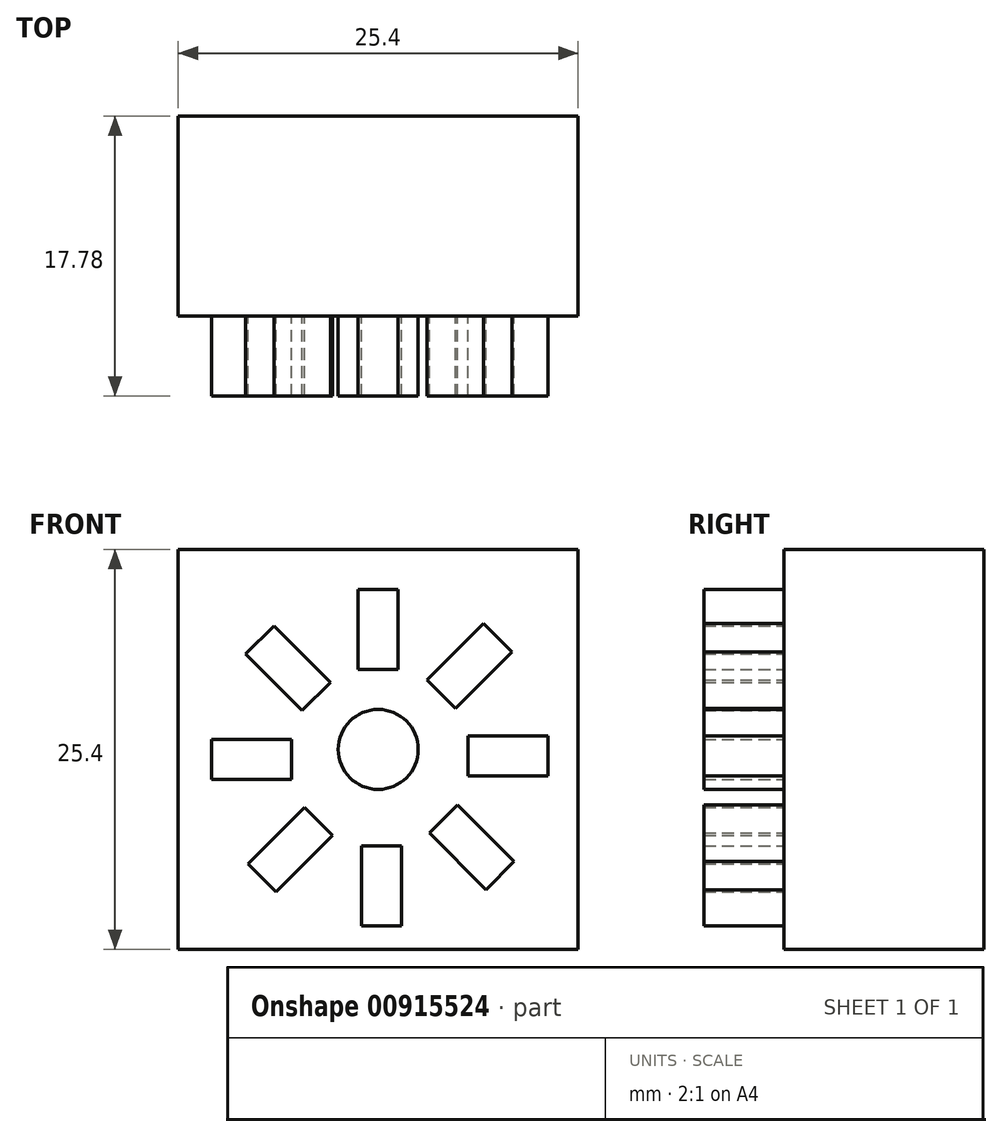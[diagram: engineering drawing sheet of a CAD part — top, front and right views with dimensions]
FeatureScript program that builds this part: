
annotation { "Feature Type Name" : "Feature", "Feature Type Description" : "" }
export const myFeature = defineFeature(function(context is Context, id is Id, definition is map)
    precondition{}
    {
        {
            var Q0;
            Q0=qCreatedBy(makeId("Front.planeOp"),FACE);
            var sketch = newSketch(context, id + "F0", { "sketchPlane" : qUnion([Q0])});
            skLineSegment(sketch, "E0.bottom", {"start": v(5.5, 14.4) * mm, "end": v(-19.9, 14.4) * mm});
            skLineSegment(sketch, "E0.top", {"start": v(5.5, -11) * mm, "end": v(-19.9, -11) * mm});
            skLineSegment(sketch, "E0.left", {"start": v(5.5, 14.4) * mm, "end": v(5.5, -11) * mm});
            skLineSegment(sketch, "E0.right", {"start": v(-19.9, 14.4) * mm, "end": v(-19.9, -11) * mm});
            skSolve(sketch);
        }
        {
            var Q0;
            Q0 = qSketchRegion(id + "F0", true);
            extrude(context, id + "F1", {"entities" : qUnion([Q0]), "depth" : 12.7 * mm, "offsetDistance" : 25.4 * mm});
        }
        {
            var Q0;
            Q0=qCreatedBy(makeId("Front.planeOp"),FACE);
            var sketch = newSketch(context, id + "F2", { "sketchPlane" : qUnion([Q0])});
            skLineSegment(sketch, "E1", {"start": v(-7.2, 14.4) * mm, "end": v(-7.2, -12.07) * mm, "construction": true});
            skLineSegment(sketch, "E2", {"start": v(-32.91, 1.7) * mm, "end": v(5.5, 1.7) * mm, "construction": true});
            skSolve(sketch);
        }
        {
            var Q0;
            Q0=makeQuery(id+"F1.opExtrude","CAP_FACE",FACE,{"disambiguationData":[OSD([sQuery(id+"F0.wireOp",EDGE,"E0.bottom"),sQuery(id+"F0.wireOp",EDGE,"E0.top"),sQuery(id+"F0.wireOp",EDGE,"E0.left"),sQuery(id+"F0.wireOp",EDGE,"E0.right")])],"isStart":false});
            var sketch = newSketch(context, id + "F3", { "sketchPlane" : qUnion([Q0])});
            skCircle(sketch, "E3", {"center": v(-7.2, 1.7) * mm, "radius": 2.54 * mm});
            skSolve(sketch);
        }
        {
            var Q0;
            Q0 = qSketchRegion(id + "F3", true);
            extrude(context, id + "F4", {"entities" : qUnion([Q0]), "operationType" : NewBodyOperationType.ADD, "depth" : 5.08 * mm, "offsetDistance" : 25.4 * mm});
        }
        {
            var Q0;
            Q0=makeQuery(id+"F1.opExtrude","CAP_FACE",FACE,{"disambiguationData":[OSD([sQuery(id+"F0.wireOp",EDGE,"E0.bottom"),sQuery(id+"F0.wireOp",EDGE,"E0.top"),sQuery(id+"F0.wireOp",EDGE,"E0.left"),sQuery(id+"F0.wireOp",EDGE,"E0.right")])],"isStart":false});
            var sketch = newSketch(context, id + "F5", { "sketchPlane" : qUnion([Q0])});
            skLineSegment(sketch, "E4.bottom", {"start": v(-8.47, 11.85) * mm, "end": v(-5.93, 11.85) * mm});
            skLineSegment(sketch, "E4.top", {"start": v(-8.47, 6.77) * mm, "end": v(-5.93, 6.77) * mm});
            skLineSegment(sketch, "E4.left", {"start": v(-8.47, 11.85) * mm, "end": v(-8.47, 6.77) * mm});
            skLineSegment(sketch, "E4.right", {"start": v(-5.93, 11.85) * mm, "end": v(-5.93, 6.77) * mm});
            skSolve(sketch);
        }
        {
            var Q0;
            Q0=sQuery(id+"F2.wireOp",EDGE,"E1");
            cPlane(context, id + "F6", {"entities" : qUnion([Q0]), "cplaneType" : CPlaneType.MID_PLANE, "offset" : 25.4 * mm, "width" : 152.4 * mm, "height" : 152.4 * mm});
        }
        {
            var Q0;
            Q0=qCreatedBy(id+"F6.planeOp",FACE);
            var sketch = newSketch(context, id + "F7", { "sketchPlane" : qUnion([Q0])});
            skLineSegment(sketch, "E5", {"start": v(-7.1, 0) * mm, "end": v(-7.1, 56.2) * mm});
            skSolve(sketch);
        }
        {
            var Q0;
            Q0 = qSketchRegion(id + "F5", true);
            extrude(context, id + "F8", {"entities" : qUnion([Q0]), "depth" : 5.08 * mm, "offsetDistance" : 25.4 * mm});
        }
        {
            var Q0;
            Q0=makeQuery(id+"F8.opExtrude","SWEPT_BODY",BODY,{"disambiguationData":[OSD([sQuery(id+"F5.wireOp",EDGE,"E4.bottom"),sQuery(id+"F5.wireOp",EDGE,"E4.top"),sQuery(id+"F5.wireOp",EDGE,"E4.left"),sQuery(id+"F5.wireOp",EDGE,"E4.right")])]});
            var Q1;
            Q1=sQuery(id+"F7.wireOp",EDGE,"E5");
            circularPattern(context, id + "F9", {"entities" : qUnion([Q0]), "axis" : qUnion([Q1]), "angle" : 360 * degree, "instanceCount" : 8, "equalSpace" : true});
        }
    });
